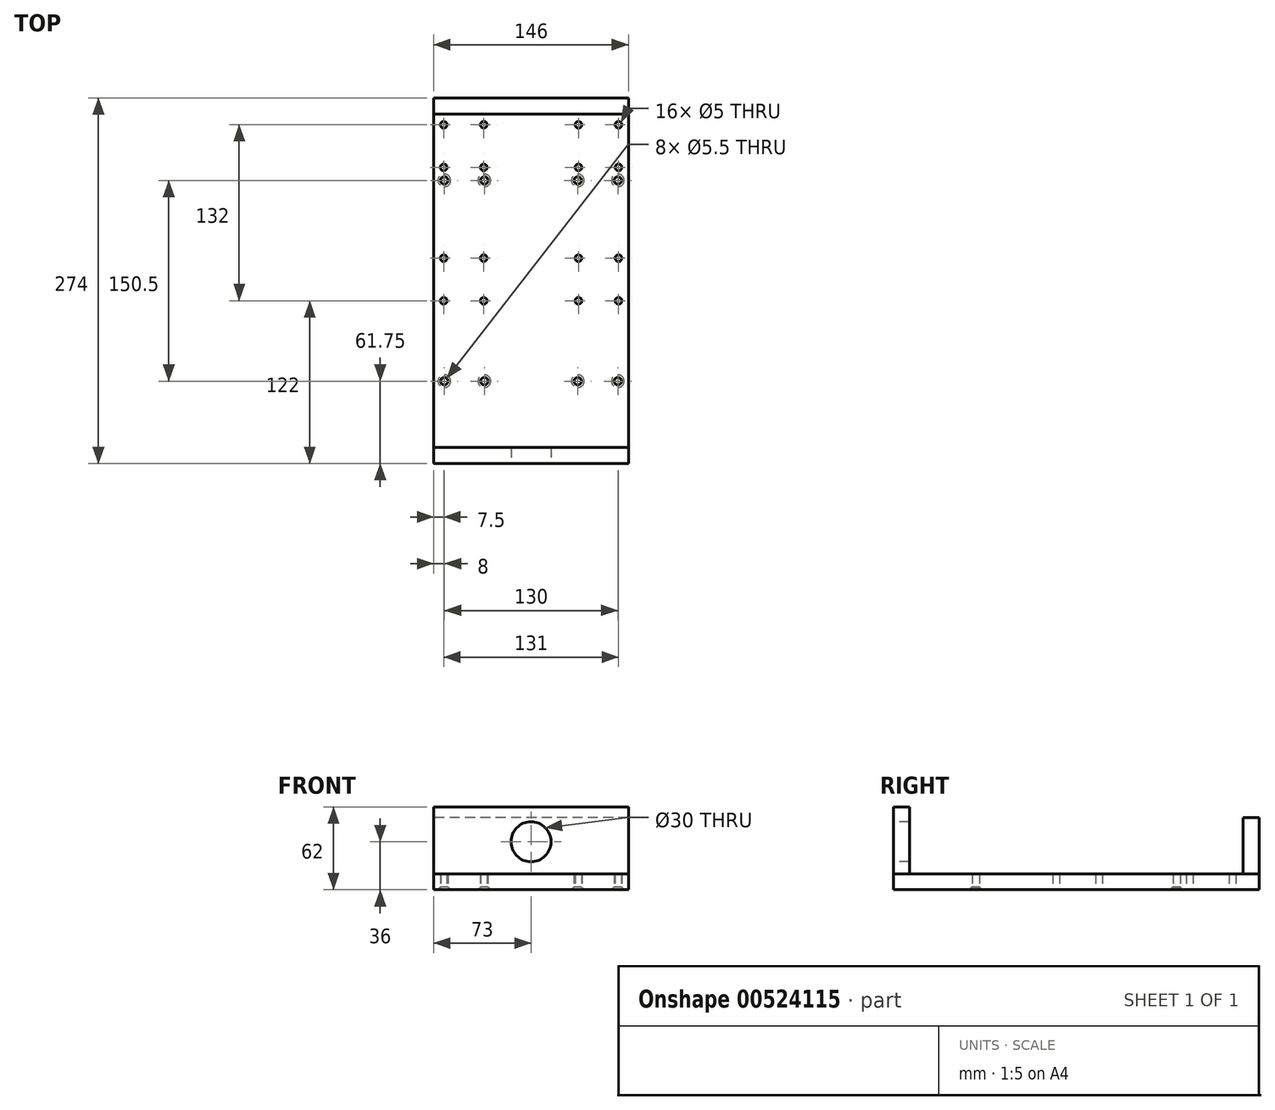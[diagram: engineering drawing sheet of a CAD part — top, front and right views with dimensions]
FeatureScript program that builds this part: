
annotation { "Feature Type Name" : "Feature", "Feature Type Description" : "" }
export const myFeature = defineFeature(function(context is Context, id is Id, definition is map)
    precondition{}
    {
        {
            var Q0;
            Q0=qCreatedBy(makeId("Top.planeOp"),FACE);
            var sketch = newSketch(context, id + "F0", { "sketchPlane" : qUnion([Q0])});
            skLineSegment(sketch, "E0.bottom", {"start": v(73, 137) * mm, "end": v(-73, 137) * mm});
            skLineSegment(sketch, "E0.top", {"start": v(73, -137) * mm, "end": v(-73, -137) * mm});
            skLineSegment(sketch, "E0.left", {"start": v(73, 137) * mm, "end": v(73, -137) * mm});
            skLineSegment(sketch, "E0.right", {"start": v(-73, 137) * mm, "end": v(-73, -137) * mm});
            skPoint(sketch, "E0.middle", {"position": v(0, 0) * mm});
            skLineSegment(sketch, "E1", {"start": v(0, 0) * mm, "end": v(73, 0) * mm, "construction": true});
            skLineSegment(sketch, "E2", {"start": v(0, 0) * mm, "end": v(0, 137) * mm, "construction": true});
            skLineSegment(sketch, "E3", {"start": v(0, 0) * mm, "end": v(0, -137) * mm, "construction": true});
            skPoint(sketch, "E4", {"position": v(65, 75.25) * mm});
            skCircle(sketch, "E5", {"center": v(65, 75.25) * mm, "radius": 2.75 * mm});
            skPoint(sketch, "E6.MirrorP", {"position": v(65, -75.25) * mm});
            skCircle(sketch, "E7.MirrorC", {"center": v(65, -75.25) * mm, "radius": 2.75 * mm});
            skPoint(sketch, "E8", {"position": v(35, 75.25) * mm});
            skCircle(sketch, "E9", {"center": v(35, 75.25) * mm, "radius": 2.75 * mm});
            skPoint(sketch, "E10.MirrorP", {"position": v(35, -75.25) * mm});
            skCircle(sketch, "E11.MirrorC", {"center": v(35, -75.25) * mm, "radius": 2.75 * mm});
            skCircle(sketch, "E12.MirrorC", {"center": v(-35, 75.25) * mm, "radius": 2.75 * mm});
            skCircle(sketch, "E13.MirrorC", {"center": v(-65, 75.25) * mm, "radius": 2.75 * mm});
            skCircle(sketch, "E14.MirrorC", {"center": v(-35, -75.25) * mm, "radius": 2.75 * mm});
            skCircle(sketch, "E15.MirrorC", {"center": v(-65, -75.25) * mm, "radius": 2.75 * mm});
            skLineSegment(sketch, "E16", {"start": v(0, 0) * mm, "end": v(0, 72.5) * mm, "construction": true});
            skLineSegment(sketch, "E17", {"start": v(0, 0) * mm, "end": v(0, -72.5) * mm, "construction": true});
            skLineSegment(sketch, "E18", {"start": v(0, 117) * mm, "end": v(73, 117) * mm, "construction": true});
            skLineSegment(sketch, "E19", {"start": v(0, 85) * mm, "end": v(73, 85) * mm, "construction": true});
            skLineSegment(sketch, "E20", {"start": v(65.5, 117) * mm, "end": v(65.5, 51) * mm, "construction": true});
            skLineSegment(sketch, "E21", {"start": v(35.5, 117) * mm, "end": v(35.5, 51) * mm, "construction": true});
            skPoint(sketch, "E22", {"position": v(35.5, 117) * mm});
            skPoint(sketch, "E23", {"position": v(35.5, 85) * mm});
            skPoint(sketch, "E24", {"position": v(65.5, 85) * mm});
            skPoint(sketch, "E25", {"position": v(65.5, 117) * mm});
            skCircle(sketch, "E26", {"center": v(35.5, 117) * mm, "radius": 2.5 * mm});
            skCircle(sketch, "E27", {"center": v(35.5, 85) * mm, "radius": 2.5 * mm});
            skCircle(sketch, "E28", {"center": v(65.5, 85) * mm, "radius": 2.5 * mm});
            skCircle(sketch, "E29", {"center": v(65.5, 117) * mm, "radius": 2.5 * mm});
            skCircle(sketch, "E30.MirrorC", {"center": v(35.5, 17) * mm, "radius": 2.5 * mm});
            skPoint(sketch, "E31.MirrorP", {"position": v(65.5, 17) * mm});
            skCircle(sketch, "E32.MirrorC", {"center": v(65.5, 17) * mm, "radius": 2.5 * mm});
            skPoint(sketch, "E33.MirrorP", {"position": v(35.5, -15) * mm});
            skCircle(sketch, "E34.MirrorC", {"center": v(35.5, -15) * mm, "radius": 2.5 * mm});
            skCircle(sketch, "E35.MirrorC", {"center": v(65.5, -15) * mm, "radius": 2.5 * mm});
            skCircle(sketch, "E36.MirrorC", {"center": v(-35.5, 117) * mm, "radius": 2.5 * mm});
            skCircle(sketch, "E37.MirrorC", {"center": v(-65.5, 117) * mm, "radius": 2.5 * mm});
            skCircle(sketch, "E38.MirrorC", {"center": v(-65.5, 85) * mm, "radius": 2.5 * mm});
            skCircle(sketch, "E39.MirrorC", {"center": v(-35.5, 85) * mm, "radius": 2.5 * mm});
            skCircle(sketch, "E40.MirrorC", {"center": v(-35.5, 17) * mm, "radius": 2.5 * mm});
            skPoint(sketch, "E41.MirrorP", {"position": v(-65.5, 17) * mm});
            skCircle(sketch, "E42.MirrorC", {"center": v(-65.5, 17) * mm, "radius": 2.5 * mm});
            skCircle(sketch, "E43.MirrorC", {"center": v(-65.5, -15) * mm, "radius": 2.5 * mm});
            skCircle(sketch, "E44.MirrorC", {"center": v(-35.5, -15) * mm, "radius": 2.5 * mm});
            skSolve(sketch);
        }
        {
            var Q0;
            Q0=makeQuery(id+"F0.imprint","IMPRINT",FACE,{"disambiguationData":[TD([[makeQuery(id+"F0.imprint","IMPRINT",EDGE,{"derivedFrom":sQuery(id+"F0.wireOp",EDGE,"E0.bottom")}),1.0]])]});
            extrude(context, id + "F1", {"entities" : qUnion([Q0]), "depth" : 12 * mm, "offsetDistance" : 25 * mm});
        }
        {
            var Q0;
            Q0=qCreatedBy(makeId("Front.planeOp"),FACE);
            cPlane(context, id + "F2", {"entities" : qUnion([Q0]), "cplaneType" : CPlaneType.OFFSET, "offset" : (274 / 2) * mm, "width" : 150 * mm, "height" : 150 * mm});
        }
        {
            var Q0;
            Q0=qCreatedBy(makeId("Front.planeOp"),FACE);
            cPlane(context, id + "F3", {"entities" : qUnion([Q0]), "cplaneType" : CPlaneType.OFFSET, "offset" : (274 / 2) * mm, "oppositeDirection" : true, "width" : 150 * mm, "height" : 150 * mm});
        }
        {
            var Q0;
            Q0=qCreatedBy(id+"F2.planeOp",FACE);
            var sketch = newSketch(context, id + "F4", { "sketchPlane" : qUnion([Q0])});
            skLineSegment(sketch, "E45", {"start": v(0, 0) * mm, "end": v(0, 12) * mm, "construction": true});
            skPoint(sketch, "E46", {"position": v(0, 12) * mm});
            skLineSegment(sketch, "E47", {"start": v(0, 12) * mm, "end": v(73, 12) * mm});
            skLineSegment(sketch, "E48", {"start": v(73, 62) * mm, "end": v(0, 62) * mm});
            skLineSegment(sketch, "E49", {"start": v(73, 62) * mm, "end": v(73, 12) * mm});
            skLineSegment(sketch, "E50.MirrorCS", {"start": v(0, 12) * mm, "end": v(-73, 12) * mm});
            skLineSegment(sketch, "E51.MirrorCS", {"start": v(-73, 62) * mm, "end": v(-73, 12) * mm});
            skLineSegment(sketch, "E52.MirrorCS", {"start": v(-73, 62) * mm, "end": v(0, 62) * mm});
            skLineSegment(sketch, "E53", {"start": v(0, 12) * mm, "end": v(0, 36) * mm, "construction": true});
            skPoint(sketch, "E54", {"position": v(0, 36) * mm});
            skCircle(sketch, "E55", {"center": v(0, 36) * mm, "radius": 15 * mm});
            skSolve(sketch);
        }
        {
            var Q0;
            Q0=makeQuery(id+"F4.imprint","IMPRINT",FACE,{"disambiguationData":[TD([[makeQuery(id+"F4.imprint","IMPRINT",EDGE,{"derivedFrom":sQuery(id+"F4.wireOp",EDGE,"E47")}),1.0]])]});
            extrude(context, id + "F5", {"entities" : qUnion([Q0]), "oppositeDirection" : true, "depth" : 12 * mm, "offsetDistance" : 25 * mm});
        }
        {
            var Q0;
            Q0=qCreatedBy(id+"F3.planeOp",FACE);
            var sketch = newSketch(context, id + "F6", { "sketchPlane" : qUnion([Q0])});
            skLineSegment(sketch, "E56", {"start": v(0, 0) * mm, "end": v(0, 12) * mm, "construction": true});
            skPoint(sketch, "E57", {"position": v(0, 12) * mm});
            skLineSegment(sketch, "E58", {"start": v(0, 12) * mm, "end": v(0, 37) * mm, "construction": true});
            skLineSegment(sketch, "E59", {"start": v(0, 12) * mm, "end": v(-73, 12) * mm});
            skLineSegment(sketch, "E60", {"start": v(-73, 12) * mm, "end": v(-73, 54) * mm});
            skLineSegment(sketch, "E61", {"start": v(-73, 54) * mm, "end": v(0, 54) * mm});
            skLineSegment(sketch, "E62.MirrorCS", {"start": v(0, 12) * mm, "end": v(73, 12) * mm});
            skLineSegment(sketch, "E63.MirrorCS", {"start": v(73, 12) * mm, "end": v(73, 54) * mm});
            skLineSegment(sketch, "E64.MirrorCS", {"start": v(73, 54) * mm, "end": v(0, 54) * mm});
            skSolve(sketch);
        }
        {
            var Q0;
            Q0=makeQuery(id+"F6.imprint","IMPRINT",FACE,{"disambiguationData":[TD([[makeQuery(id+"F6.imprint","IMPRINT",EDGE,{"derivedFrom":sQuery(id+"F6.wireOp",EDGE,"E59")}),-1.0]])]});
            extrude(context, id + "F7", {"entities" : qUnion([Q0]), "depth" : 12 * mm, "offsetDistance" : 25 * mm});
        }
        {
            var Q0;
            Q0=makeQuery(id+"F1.opExtrude","CAP_EDGE",EDGE,{"disambiguationData":[OSD([sQuery(id+"F0.wireOp",EDGE,"E15.MirrorC")])],"isStart":true});
            var Q1;
            Q1=makeQuery(id+"F1.opExtrude","CAP_EDGE",EDGE,{"disambiguationData":[OSD([sQuery(id+"F0.wireOp",EDGE,"E14.MirrorC")])],"isStart":true});
            var Q2;
            Q2=makeQuery(id+"F1.opExtrude","CAP_EDGE",EDGE,{"disambiguationData":[OSD([sQuery(id+"F0.wireOp",EDGE,"E11.MirrorC")])],"isStart":true});
            var Q3;
            Q3=makeQuery(id+"F1.opExtrude","CAP_EDGE",EDGE,{"disambiguationData":[OSD([sQuery(id+"F0.wireOp",EDGE,"E7.MirrorC")])],"isStart":true});
            var Q4;
            Q4=makeQuery(id+"F1.opExtrude","CAP_EDGE",EDGE,{"disambiguationData":[OSD([sQuery(id+"F0.wireOp",EDGE,"E5")])],"isStart":true});
            var Q5;
            Q5=makeQuery(id+"F1.opExtrude","CAP_EDGE",EDGE,{"disambiguationData":[OSD([sQuery(id+"F0.wireOp",EDGE,"E9")])],"isStart":true});
            var Q6;
            Q6=makeQuery(id+"F1.opExtrude","CAP_EDGE",EDGE,{"disambiguationData":[OSD([sQuery(id+"F0.wireOp",EDGE,"E12.MirrorC")])],"isStart":true});
            var Q7;
            Q7=makeQuery(id+"F1.opExtrude","CAP_EDGE",EDGE,{"disambiguationData":[OSD([sQuery(id+"F0.wireOp",EDGE,"E13.MirrorC")])],"isStart":true});
            chamfer(context, id + "F8", {"entities" : qUnion([Q0, Q1, Q2, Q3, Q4, Q5, Q6, Q7]), "width" : 2 * mm, "tangentPropagation" : true});
        }
    });
